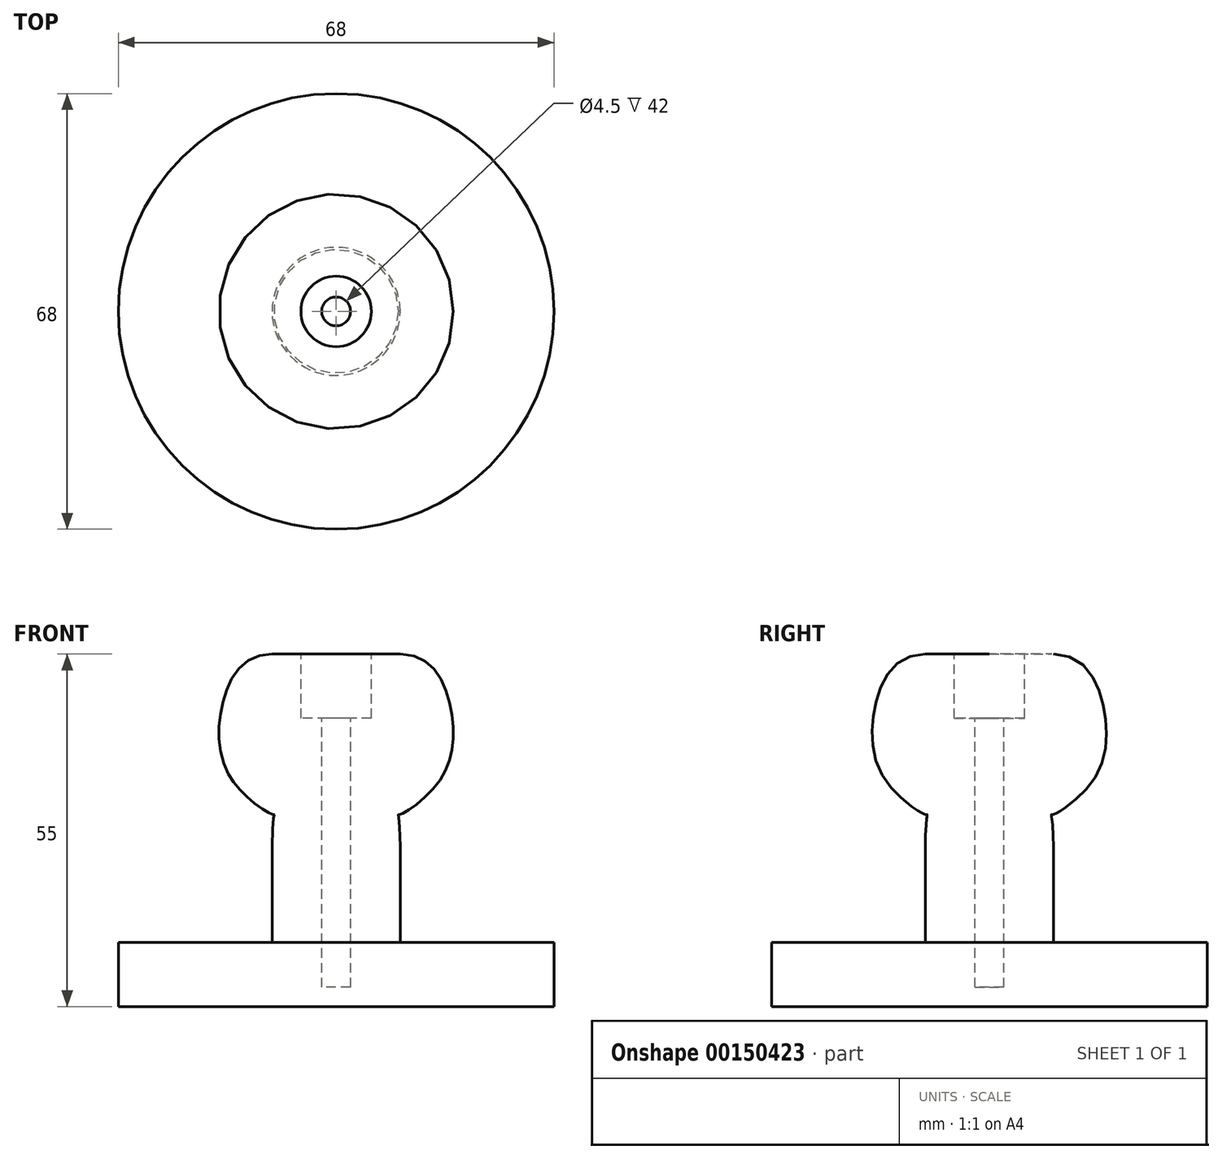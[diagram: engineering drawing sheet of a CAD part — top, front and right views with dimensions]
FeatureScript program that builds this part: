
annotation { "Feature Type Name" : "Feature", "Feature Type Description" : "" }
export const myFeature = defineFeature(function(context is Context, id is Id, definition is map)
    precondition{}
    {
        {
            var Q0;
            Q0=qCreatedBy(makeId("Front.planeOp"),FACE);
            var sketch = newSketch(context, id + "F0", { "sketchPlane" : qUnion([Q0])});
            skLineSegment(sketch, "E0", {"start": v(0, -10) * mm, "end": v(34, -10) * mm});
            skLineSegment(sketch, "E1", {"start": v(34, -10) * mm, "end": v(34, 0) * mm});
            skLineSegment(sketch, "E2", {"start": v(34, 0) * mm, "end": v(10, 0) * mm});
            skLineSegment(sketch, "E3", {"start": v(10, 0) * mm, "end": v(10, 15) * mm});
            skFitSpline(sketch, "E4", {"points": [v(10, 15) * mm, v(10, 20) * mm, v(16, 25) * mm, v(18, 36) * mm, v(10, 45) * mm], "startDerivative": vector(0, 92.95) * mm, "endDerivative": vector(-54.62, 0) * mm});
            skLineSegment(sketch, "E5", {"start": v(10, 45) * mm, "end": v(5.5, 45) * mm});
            skLineSegment(sketch, "E6", {"start": v(0, -7) * mm, "end": v(0, -10) * mm});
            skLineSegment(sketch, "E7", {"start": v(5.5, 45) * mm, "end": v(5.5, 35) * mm});
            skLineSegment(sketch, "E8", {"start": v(5.5, 35) * mm, "end": v(2.25, 35) * mm});
            skLineSegment(sketch, "E9", {"start": v(2.25, 35) * mm, "end": v(2.25, -7) * mm});
            skLineSegment(sketch, "E10", {"start": v(2.25, -7) * mm, "end": v(0, -7) * mm});
            skLineSegment(sketch, "E11", {"start": v(5.5, 45) * mm, "end": v(0, 45) * mm, "construction": true});
            skLineSegment(sketch, "E12", {"start": v(0, 45) * mm, "end": v(0, -7) * mm, "construction": true});
            skSolve(sketch);
        }
        {
            var Q0;
            Q0 = qSketchRegion(id + "F0", true);
            var Q1;
            Q1=sQuery(id+"F0.wireOp",EDGE,"E5");
            var Q2;
            Q2=sQuery(id+"F0.wireOp",EDGE,"E4");
            var Q3;
            Q3=sQuery(id+"F0.wireOp",EDGE,"E3");
            var Q4;
            Q4=sQuery(id+"F0.wireOp",EDGE,"E2");
            var Q5;
            Q5=sQuery(id+"F0.wireOp",EDGE,"E1");
            var Q6;
            Q6=sQuery(id+"F0.wireOp",EDGE,"E0");
            var Q7;
            Q7=sQuery(id+"F0.wireOp",EDGE,"E6");
            revolve(context, id + "F1", {"entities" : qUnion([Q0]), "surfaceEntities" : qUnion([Q1, Q2, Q3, Q4, Q5, Q6]), "axis" : qUnion([Q7]), "revolveType" : RevolveType.FULL});
        }
    });
